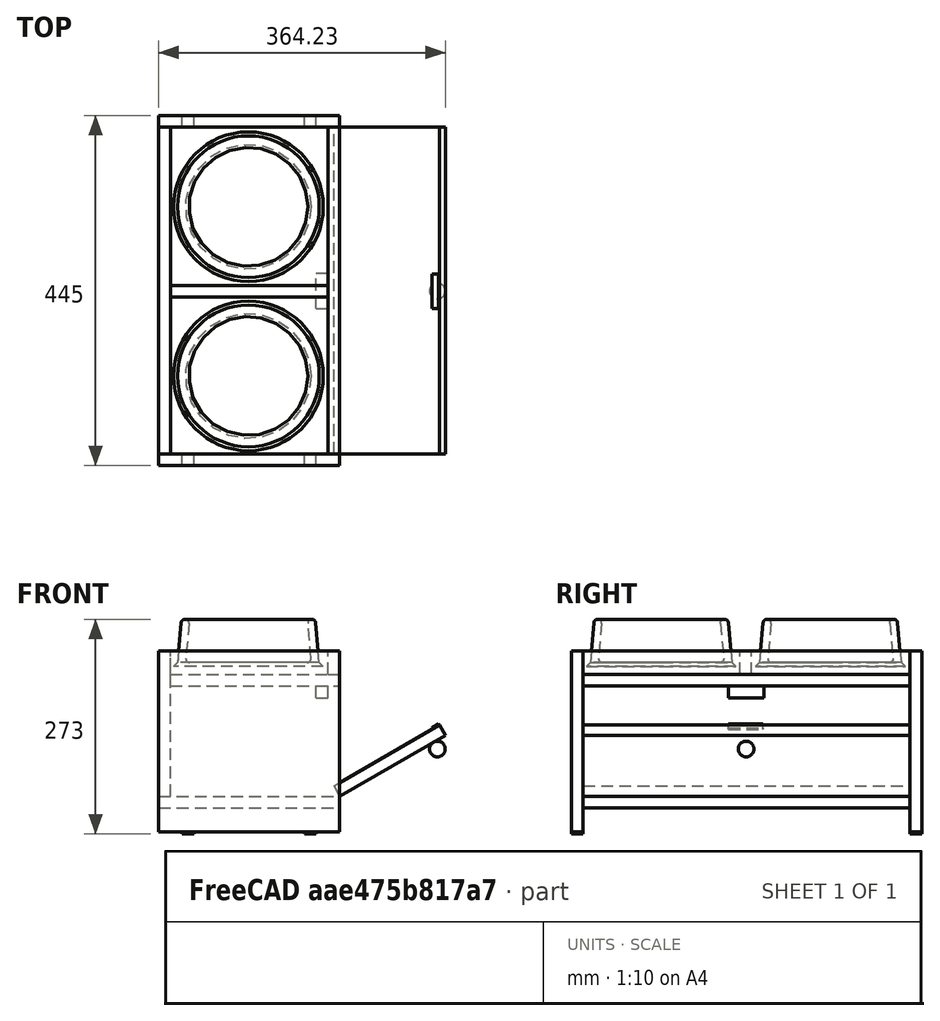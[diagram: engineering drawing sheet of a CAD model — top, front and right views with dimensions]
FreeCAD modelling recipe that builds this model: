
FCSTD DOCUMENT  (FreeCAD 0.17R13522 (Git))
Label: SuporteParaComedouroComComedouros
License: All rights reserved
LicenseURL: http://en.wikipedia.org/wiki/All_rights_reserved
objects: Part::Box×14, Part::Cone×6, Part::Fillet×4, Part::Cut×2, Part::MultiFuse×2, Part::Sphere×1
note: 29 computed .brp shape members not serialized (recipe doc carries the construction recipe); baked Part::Feature solids carry a one-line shape summary decoded from their .brp

FEATURE [Part::Box] Box  label="SuporteLateralVerticalEsquerdo"
  AttacherType = Attacher::AttachEngine3D
  Height = 230
  Length = 230
  Width = 15
FEATURE [Part::Box] Box001  label="TampoSuperiorHorizontal"
  AttacherType = Attacher::AttachEngine3D
  Height = 15
  Length = 215
  Placement = pos=(15,15,185) rot=(0,0,1;0rad)
  Width = 415
FEATURE [Part::Box] Box002  label="SuporteLateralVerticalDireito"
  AttacherType = Attacher::AttachEngine3D
  Height = 230
  Length = 230
  Placement = pos=(0,430,0) rot=(0,0,1;0rad)
  Width = 15
FEATURE [Part::Box] Box003  label="SuporteVerticalMeio"
  AttacherType = Attacher::AttachEngine3D
  Height = 30
  Length = 200
  Placement = pos=(15,214,200) rot=(0,0,1;0rad)
  Width = 15
FEATURE [Part::Box] Box005  label="SuporteFrenteSuperiorVertical"
  AttacherType = Attacher::AttachEngine3D
  Height = 30
  Length = 15
  Placement = pos=(215,15,200) rot=(0,0,1;0rad)
  Width = 415
FEATURE [Part::Box] Box006  label="SuporteFundoInferiorVertical"
  AttacherType = Attacher::AttachEngine3D
  Height = 185
  Length = 15
  Placement = pos=(0,15,45) rot=(0,0,1;0rad)
  Width = 415
FEATURE [Part::Box] Box007  label="TampoInferiorHorizontal"
  AttacherType = Attacher::AttachEngine3D
  Height = 15
  Length = 230
  Placement = pos=(0,15,30) rot=(0,0,1;0rad)
  Width = 415
FEATURE [Part::Box] Box008  label="TampaBasculante"
  AttacherType = Attacher::AttachEngine3D
  Height = 155
  Length = 15
  Placement = pos=(222.5,15,58) rot=(0,1,0;1.0472rad)
  Width = 415
FEATURE [Part::Box] Box010  label="ImaDaMesa SuperiorHorizontal"
  AttacherType = Attacher::AttachEngine3D
  Height = 15
  Length = 15
  Placement = pos=(200,199.5,170) rot=(0,0,1;0rad)
  Width = 45
FEATURE [Part::Box] Box011  label="ChapaDoIma"
  AttacherType = Attacher::AttachEngine3D
  Height = 10
  Length = 2
  Placement = pos=(347,199.5,132) rot=(0,1,0;1.0472rad)
  Width = 44
FEATURE [Part::Cone] Cone  label="BaseComedouroAgua"
  Angle = 360
  AttacherType = Attacher::AttachEngine3D
  Height = 5
  Placement = pos=(114,114,400) rot=(0,0,1;0rad)
  Radius1 = 95
  Radius2 = 90
FEATURE [Part::Cone] Cone001
  Angle = 360
  AttacherType = Attacher::AttachEngine3D
  Height = 55
  Placement = pos=(114,114,405) rot=(0,0,1;0rad)
  Radius1 = 90
  Radius2 = 85
FEATURE [Part::Cone] Cone002
  Angle = 360
  AttacherType = Attacher::AttachEngine3D
  Height = 55
  Placement = pos=(114,114,405) rot=(0,0,1;0rad)
  Radius1 = 80
  Radius2 = 75
FEATURE [Part::Cut] Cut  label="ComedouroAgua000"
  Base = -> Cone001
  Tool = -> Cone002
FEATURE [Part::Fillet] Fillet
  Base = -> Cut
  Edges = 2 edges r=4.9: [Edge1,Edge4]
FEATURE [Part::MultiFuse] Fusion  label="ComedouroAgua003"
  Placement = pos=(0,0,-190) rot=(0,0,1;0rad)
  Shapes = -> [Cone,Fillet]
FEATURE [Part::Cone] Cone003  label="BaseComedouroAgua001"
  Angle = 360
  AttacherType = Attacher::AttachEngine3D
  Height = 5
  Placement = pos=(114,114,400) rot=(0,0,1;0rad)
  Radius1 = 95
  Radius2 = 90
FEATURE [Part::Cone] Cone004
  Angle = 360
  AttacherType = Attacher::AttachEngine3D
  Height = 55
  Placement = pos=(114,114,405) rot=(0,0,1;0rad)
  Radius1 = 80
  Radius2 = 75
FEATURE [Part::Cone] Cone005
  Angle = 360
  AttacherType = Attacher::AttachEngine3D
  Height = 55
  Placement = pos=(114,114,405) rot=(0,0,1;0rad)
  Radius1 = 90
  Radius2 = 85
FEATURE [Part::Cut] Cut001  label="ComedouroAgua002"
  Base = -> Cone005
  Tool = -> Cone004
FEATURE [Part::Fillet] Fillet001
  Base = -> Cut001
  Edges = 2 edges r=4.9: [Edge1,Edge4]
FEATURE [Part::MultiFuse] Fusion001  label="ComedouroRacao000"
  Placement = pos=(0,215,-190) rot=(0,0,1;0rad)
  Shapes = -> [Cone003,Fillet001]
FEATURE [Part::Sphere] Sphere  label="Puxador"
  Angle1 = -90
  Angle2 = 90
  Angle3 = 360
  AttacherType = Attacher::AttachEngine3D
  Placement = pos=(354,222,105) rot=(0,0,1;0rad)
  Radius = 10
FEATURE [Part::Fillet] Fillet002  label="ComedouroAgua"
  Base = -> Fusion
  Edges = 1 edges r=4.9: [Edge12]
FEATURE [Part::Fillet] Fillet003  label="ComedouroRacao"
  Base = -> Fusion001
  Edges = 1 edges r=4.9: [Edge12]
FEATURE [Part::Box] Box012  label="Cube"
  AttacherType = Attacher::AttachEngine3D
  Height = 3
  Length = 15
  Placement = pos=(30,0,-3) rot=(0,0,1;0rad)
  Width = 15
FEATURE [Part::Box] Box013  label="Cube001"
  AttacherType = Attacher::AttachEngine3D
  Height = 3
  Length = 15
  Placement = pos=(185,0,-3) rot=(0,0,1;0rad)
  Width = 15
FEATURE [Part::Box] Box014  label="Cube002"
  AttacherType = Attacher::AttachEngine3D
  Height = 3
  Length = 15
  Placement = pos=(30,430,-3) rot=(0,0,1;0rad)
  Width = 15
FEATURE [Part::Box] Box015  label="Cube003"
  AttacherType = Attacher::AttachEngine3D
  Height = 3
  Length = 15
  Placement = pos=(185,430,-3) rot=(0,0,1;0rad)
  Width = 15
